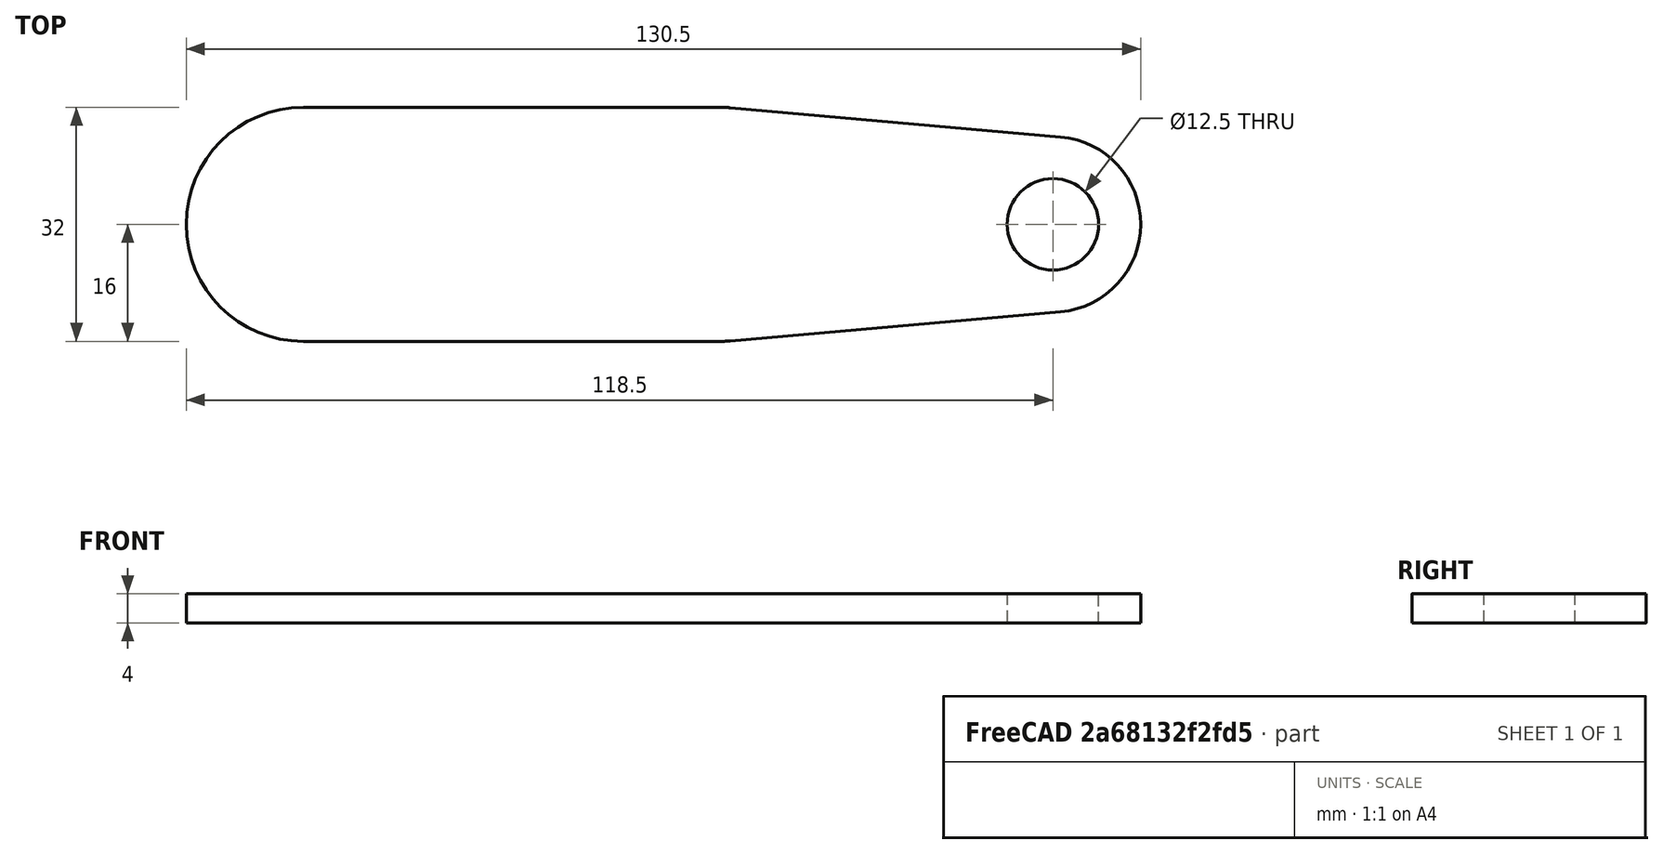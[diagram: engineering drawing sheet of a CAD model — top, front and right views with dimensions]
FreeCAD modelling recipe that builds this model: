
FCSTD DOCUMENT  (FreeCAD 0.19R24267 +99 (Git))
Label: V2 Range pin retainer plate single pin location
License: All rights reserved
LicenseURL: http://en.wikipedia.org/wiki/All_rights_reserved
objects: Sketcher::SketchObject×1, PartDesign::Pad×1, PartDesign::Body×1
note: 4 computed .brp shape members not serialized (recipe doc carries the construction recipe); baked Part::Feature solids carry a one-line shape summary decoded from their .brp

FEATURE [Sketcher::SketchObject] Sketch
  FullyConstrained = true
  MapMode = 5
  Support = -> [XY_Plane]
  sketch-geometry (10):
    g0: ArcOfCircle CenterX=0 CenterY=0 CenterZ=0 NormalX=0 NormalY=0 NormalZ=1 AngleXU=0 Radius=12 StartAngle=4.80041 EndAngle=7.76596
    g1: Circle CenterX=0 CenterY=0 CenterZ=0 NormalX=0 NormalY=0 NormalZ=1 AngleXU=0 Radius=6.25
    g2: ArcOfCircle CenterX=-102.5 CenterY=0 CenterZ=0 NormalX=0 NormalY=0 NormalZ=1 AngleXU=0 Radius=16 StartAngle=1.5708 EndAngle=4.71239
    g3: GeomPoint X=-118.5 Y=0 Z=0
    g4: ArcOfCircle CenterX=-45.5 CenterY=0 CenterZ=0 NormalX=0 NormalY=0 NormalZ=1 AngleXU=0 Radius=16 StartAngle=4.71239 EndAngle=4.80041
    g5: LineSegment StartX=-102.5 StartY=-16 StartZ=0 EndX=-45.5 EndY=-16 EndZ=0
    g6: LineSegment StartX=-102.5 StartY=16 StartZ=0 EndX=-45.5 EndY=16 EndZ=0
    g7: LineSegment StartX=-44.0934 StartY=15.9381 StartZ=0 EndX=1.05495 EndY=11.9535 EndZ=0
    g8: LineSegment StartX=-44.0934 StartY=-15.9381 StartZ=0 EndX=1.05495 EndY=-11.9535 EndZ=0
    g9: ArcOfCircle CenterX=-45.5 CenterY=0 CenterZ=0 NormalX=0 NormalY=0 NormalZ=1 AngleXU=0 Radius=16 StartAngle=1.48277 EndAngle=1.5708
  constraints (23):
    c: Coincident(g0,g-1)
    c: Radius(g0) = 12
    c: Coincident(g1,g0)
    c: PointOnObject(g2,g-1)
    c: PointOnObject(g3,g-1)
    c: PointOnObject(g3,g2)
    c: PointOnObject(g4,g-1)
    c: DistanceX(g2,g0) = 102.5
    c: DistanceX(g4,g0) = 45.5
    c: Equal(g4,g2)
    c: Horizontal(g5)
    c: Horizontal(g6)
    c: Coincident(g2,g5)
    c: Tangent(g4,g5) = -1.5708
    c: Tangent(g4,g8) = -1.5708
    c: Tangent(g9,g7) = 1.5708
    c: Coincident(g4,g9)
    c: Tangent(g0,g8) = -1.5708
    c: Tangent(g0,g7) = 1.5708
    c: Tangent(g2,g6) = 1.5708
    c: Tangent(g9,g6) = 1.5708
    c: Diameter(g1) = 12.5
    c: Diameter(g2) = 32
FEATURE [PartDesign::Pad] Pad
  Direction = (1,1,1)
  Length = 4
  Length2 = 100
  Profile = -> Sketch
  Type = 0
FEATURE [PartDesign::Body] Body
  Group = -> [Sketch,Pad]
  Origin = -> Origin
  Tip = -> Pad
